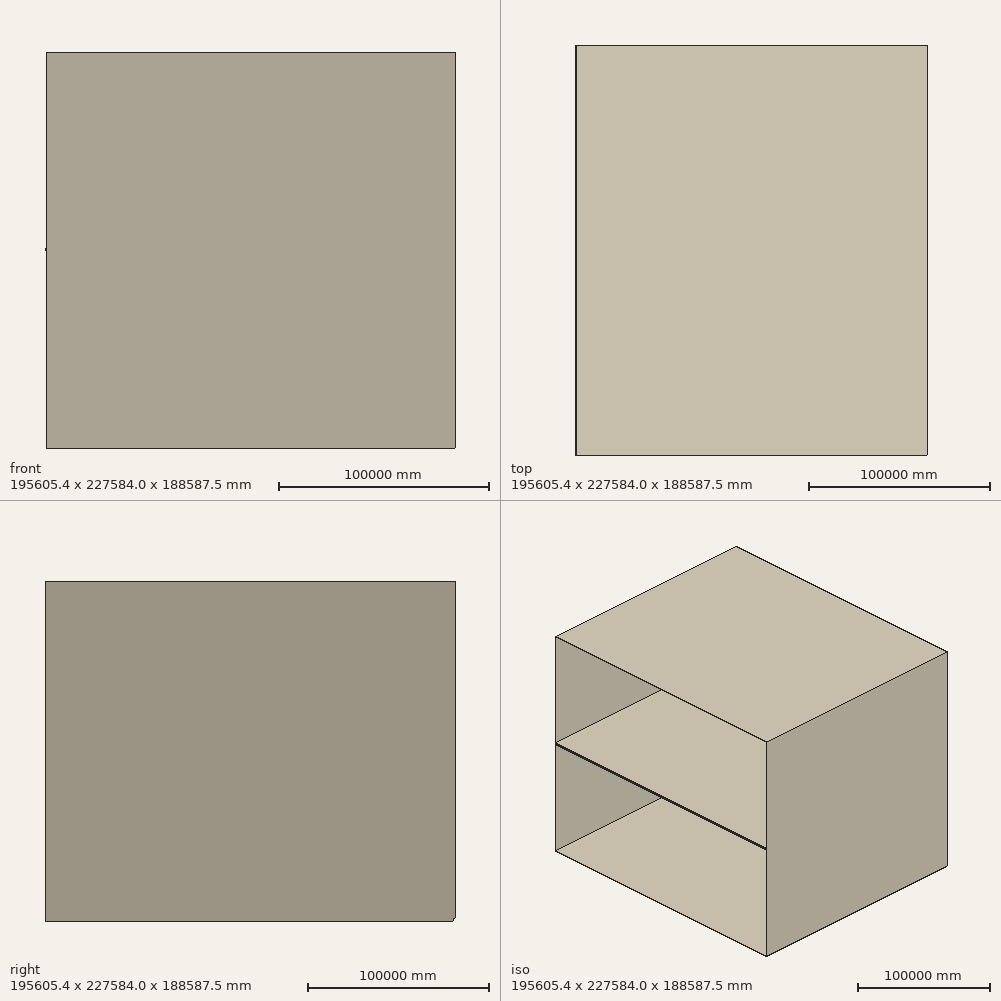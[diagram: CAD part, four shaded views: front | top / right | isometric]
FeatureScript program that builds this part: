
annotation { "Feature Type Name" : "Feature", "Feature Type Description" : "" }
export const myFeature = defineFeature(function(context is Context, id is Id, definition is map)
    precondition{}
    {
        {
            var Q0;
            Q0=qCreatedBy(makeId("Front.planeOp"),FACE);
            var sketch = newSketch(context, id + "F0", { "sketchPlane" : qUnion([Q0])});
            skLineSegment(sketch, "E0.bottom", {"start": v(97451.26, -94293.73) * mm, "end": v(-97451.26, -94293.73) * mm});
            skLineSegment(sketch, "E0.top", {"start": v(97451.26, 94293.73) * mm, "end": v(-97451.26, 94293.73) * mm});
            skLineSegment(sketch, "E0.left", {"start": v(97451.26, -94293.73) * mm, "end": v(97451.26, 94293.73) * mm});
            skLineSegment(sketch, "E0.right", {"start": v(-97451.26, -94293.73) * mm, "end": v(-97451.26, 94293.73) * mm});
            skPoint(sketch, "E0.middle", {"position": v(0, 0) * mm});
            skSolve(sketch);
        }
        {
            var Q0;
            Q0 = qSketchRegion(id + "F0", true);
            extrude(context, id + "F1", {"entities" : qUnion([Q0]), "depth" : 227584 * mm, "offsetDistance" : 25.4 * mm});
        }
        {
            var Q0;
            Q0=makeQuery(id+"F1.opExtrude","SWEPT_FACE",FACE,{"disambiguationData":[OSD([sQuery(id+"F0.wireOp",EDGE,"E0.right")])]});
            shell(context, id + "F2", {"entities" : qUnion([Q0]), "thickness" : 25.4 * mm});
        }
        {
            var Q0;
            Q0=makeQuery(id+"F2.opShell","OFFSET_FACE",FACE,{"disambiguationData":[OSD([sQuery(id+"F0.wireOp",EDGE,"E0.left")])]});
            var sketch = newSketch(context, id + "F3", { "sketchPlane" : qUnion([Q0])});
            skLineSegment(sketch, "E1.bottom", {"start": v(122.53, -92898.11) * mm, "end": v(916.28, -92898.11) * mm});
            skLineSegment(sketch, "E1.top", {"start": v(122.53, -94268.33) * mm, "end": v(916.28, -94268.33) * mm});
            skLineSegment(sketch, "E1.left", {"start": v(122.53, -92898.11) * mm, "end": v(122.53, -94268.33) * mm});
            skLineSegment(sketch, "E1.right", {"start": v(916.28, -92898.11) * mm, "end": v(916.28, -94268.33) * mm});
            skSolve(sketch);
        }
        {
            var Q0;
            Q0 = qSketchRegion(id + "F3", true);
            extrude(context, id + "F4", {"entities" : qUnion([Q0]), "operationType" : NewBodyOperationType.REMOVE, "oppositeDirection" : true, "depth" : 83.82 * mm, "offsetDistance" : 25.4 * mm});
        }
        {
            var Q0;
            Q0=makeQuery(id+"F2.opShell","OFFSET_FACE",FACE,{"disambiguationData":[OSD([sQuery(id+"F0.wireOp",EDGE,"E0.left")])]});
            var sketch = newSketch(context, id + "F5", { "sketchPlane" : qUnion([Q0])});
            skLineSegment(sketch, "E2.bottom", {"start": v(25.4, 0) * mm, "end": v(227558.6, 0) * mm});
            skLineSegment(sketch, "E2.top", {"start": v(25.4, 1142.68) * mm, "end": v(227558.6, 1142.68) * mm});
            skLineSegment(sketch, "E2.left", {"start": v(25.4, 0) * mm, "end": v(25.4, 1142.68) * mm});
            skLineSegment(sketch, "E2.right", {"start": v(227558.6, 0) * mm, "end": v(227558.6, 1142.68) * mm});
            skSolve(sketch);
        }
        {
            var Q0;
            Q0 = qSketchRegion(id + "F5", true);
            extrude(context, id + "F6", {"entities" : qUnion([Q0]), "operationType" : NewBodyOperationType.ADD, "depth" : 195580 * mm, "offsetDistance" : 25.4 * mm});
        }
        {
            var Q0;
            {var subQ1=sQuery(id+"F0.wireOp",EDGE,"E0.left");var subQ2=sQuery(id+"F0.wireOp",EDGE,"E0.top");Q0=makeQuery(id+"F6.boolean.opBoolean","SPLIT",FACE,{"disambiguationData":[TD([makeQuery(id+"F2.opShell","OFFSET_FACE",FACE,{"disambiguationData":[OSD([subQ2])]})])],"derivedFrom":makeQuery(id+"F2.opShell","OFFSET_FACE",FACE,{"disambiguationData":[OSD([subQ1])]})});}
            var sketch = newSketch(context, id + "F7", { "sketchPlane" : qUnion([Q0])});
            skLineSegment(sketch, "E3.bottom", {"start": v(530.33, 94268.33) * mm, "end": v(558.94, 94268.33) * mm});
            skLineSegment(sketch, "E3.top", {"start": v(530.33, 1142.68) * mm, "end": v(558.94, 1142.68) * mm});
            skLineSegment(sketch, "E3.left", {"start": v(530.33, 94268.33) * mm, "end": v(530.33, 1142.68) * mm});
            skLineSegment(sketch, "E3.right", {"start": v(558.94, 94268.33) * mm, "end": v(558.94, 1142.68) * mm});
            skLineSegment(sketch, "E4.bottom", {"start": v(900.2, 94268.33) * mm, "end": v(922.68, 94268.33) * mm});
            skLineSegment(sketch, "E4.top", {"start": v(900.2, 1142.68) * mm, "end": v(922.68, 1142.68) * mm});
            skLineSegment(sketch, "E4.left", {"start": v(900.2, 94268.33) * mm, "end": v(900.2, 1142.68) * mm});
            skLineSegment(sketch, "E4.right", {"start": v(922.68, 94268.33) * mm, "end": v(922.68, 1142.68) * mm});
            skSolve(sketch);
        }
        {
            var Q0;
            Q0 = qSketchRegion(id + "F7", true);
            extrude(context, id + "F8", {"entities" : qUnion([Q0]), "operationType" : NewBodyOperationType.ADD, "depth" : 889 * mm, "offsetDistance" : 25.4 * mm});
        }
    });
